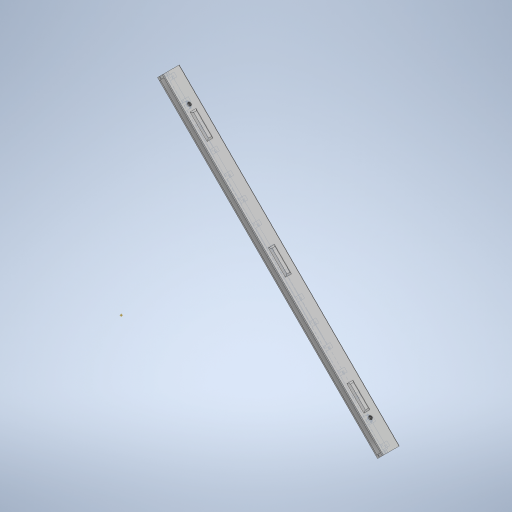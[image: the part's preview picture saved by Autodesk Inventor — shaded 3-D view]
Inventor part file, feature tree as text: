
AUTODESK INVENTOR PART (.ipt)
format: ipt  version: 2023 (Build 270158000, 158)  size: 19,173,888 bytes
history: native  units: in
note: dims shown in document units (in); Inventor stores cm internally (conversion verified against a paired STEP export)
features: move_body x4, plane x2, extrude x2, sketch x2, other x2, direct_edit x1
ambient origin geometry x8: Origin, YZ Plane, XZ Plane, XY Plane, X Axis, Y Axis, Z Axis, Center Point
bodies: Solid1 (feature_tree)
feature tree (13):
  direct_edit  "Direct Edit1"
  move_body  "Move Body1"
  move_body  "Move Body2"
  move_body  "Move Body3"
  move_body  "Move Body4"
  plane  "Work Plane1"
  extrude  "Extrusion1"  TaperAngle=0.0deg  [1 undecoded]
  plane  "Work Plane3"
  extrude  "Extrusion2"  Depth=0.1575in
  sketch  "Sketch1"  dims[d0=0.0394in d1=0.3937in d2=0.3937in d3=-57.0866in d4=-57.0866in d5=0.0in]
  sketch  "Sketch3"  dims[d6=0.3937in d7=0.0in d8=0.0in d9=0.875in d10=-3.5433in d11=0.0591in d12=0.1575in d13=0.0591in d14=0.1575in d15=6.2992in d17=0.7874in d18=0.3937in d20=0.3937in d22=6.2992in d24=0.7874in d25=0.3937in d27=0.3937in d29=0.1969in d30=0.0in d31=0.0591in d32=0.3937in d34=0.3937in d35=6.2992in d37=0.7874in d39=0.4134in d40=0.0in]
  other  "Netzkörper1"
  other  "Scale1"
note: 1 required parameter value undecoded (feature->parameter linkage not recoverable at this tier; creation-order binding heuristic only, values carry confidence <= 0.55)
